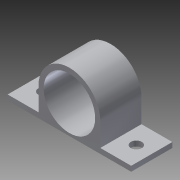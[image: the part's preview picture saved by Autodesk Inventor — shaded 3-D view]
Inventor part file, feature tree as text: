
AUTODESK INVENTOR PART (.ipt)
format: ipt  version: 2013 (Build 170138000, 138)  size: 152,576 bytes
history: native  units: in
note: dims shown in document units (in); Inventor stores cm internally (conversion verified against a paired STEP export)
features: sketch x6, extrude x2
ambient origin geometry x8: Origin, YZ Plane, XZ Plane, XY Plane, X Axis, Y Axis, Z Axis, Center Point
bodies: Solid1 (feature_tree)
feature tree (8):
  extrude  "Extrusion1"  Depth=1.5in
  extrude  "Extrusion2"  Depth=0.6875in
  sketch  "Sketch3"  dims[d4=1.25in]
  sketch  "Sketch4"  dims[d5=0.125in]
  sketch  "Sketch5"  dims[d6=1.0in d7=0.0in]
  sketch  "Sketch6"  dims[d8=0.266in d11=1.0in d12=0.0in d13=0.375in d14=0.266in d15=0.375in]
  sketch  "Sketch1"  dims[d0=1.5in d1=1.5in]
  sketch  "Sketch2"  dims[d2=0.125in d3=0.6875in]
